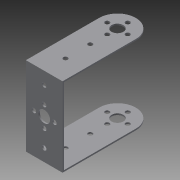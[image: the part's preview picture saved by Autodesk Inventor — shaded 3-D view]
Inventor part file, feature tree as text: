
AUTODESK INVENTOR PART (.ipt)
format: ipt  version: 2015 (Build 190159000, 159)  size: 159,744 bytes
history: native  units: mm
features: extrude x3, sketch x3, projected_geometry x1
ambient origin geometry x8: Origin, YZ Plane, XZ Plane, XY Plane, X Axis, Y Axis, Z Axis, Center Point
bodies: Solid1 (feature_tree)
feature tree (7):
  extrude  "Extrusion1"  Depth=25.0mm
  extrude  "Extrusion2"  Depth=3.0mm
  extrude  "Extrusion3"  Depth=1.0mm
  sketch  "Sketch1"  dims[d0=25.0mm d1=50.0mm]
  sketch  "Sketch2"  dims[d3=8.0mm d5=3.0mm]
  projected_geometry  "Projected Loop1"
  sketch  "Sketch3"  dims[d6=3.0mm d7=3.0mm d8=3.0mm d10=3.0mm d12=3.0mm d13=54.0mm d14=0.0mm d15=1.0mm d16=1.0mm d17=1.0mm d18=1.0mm d19=58.0mm d20=0.0mm d23=3.0mm d24=40.0mm d26=360.0deg d29=3.0mm d30=58.0mm d31=0.0mm]
